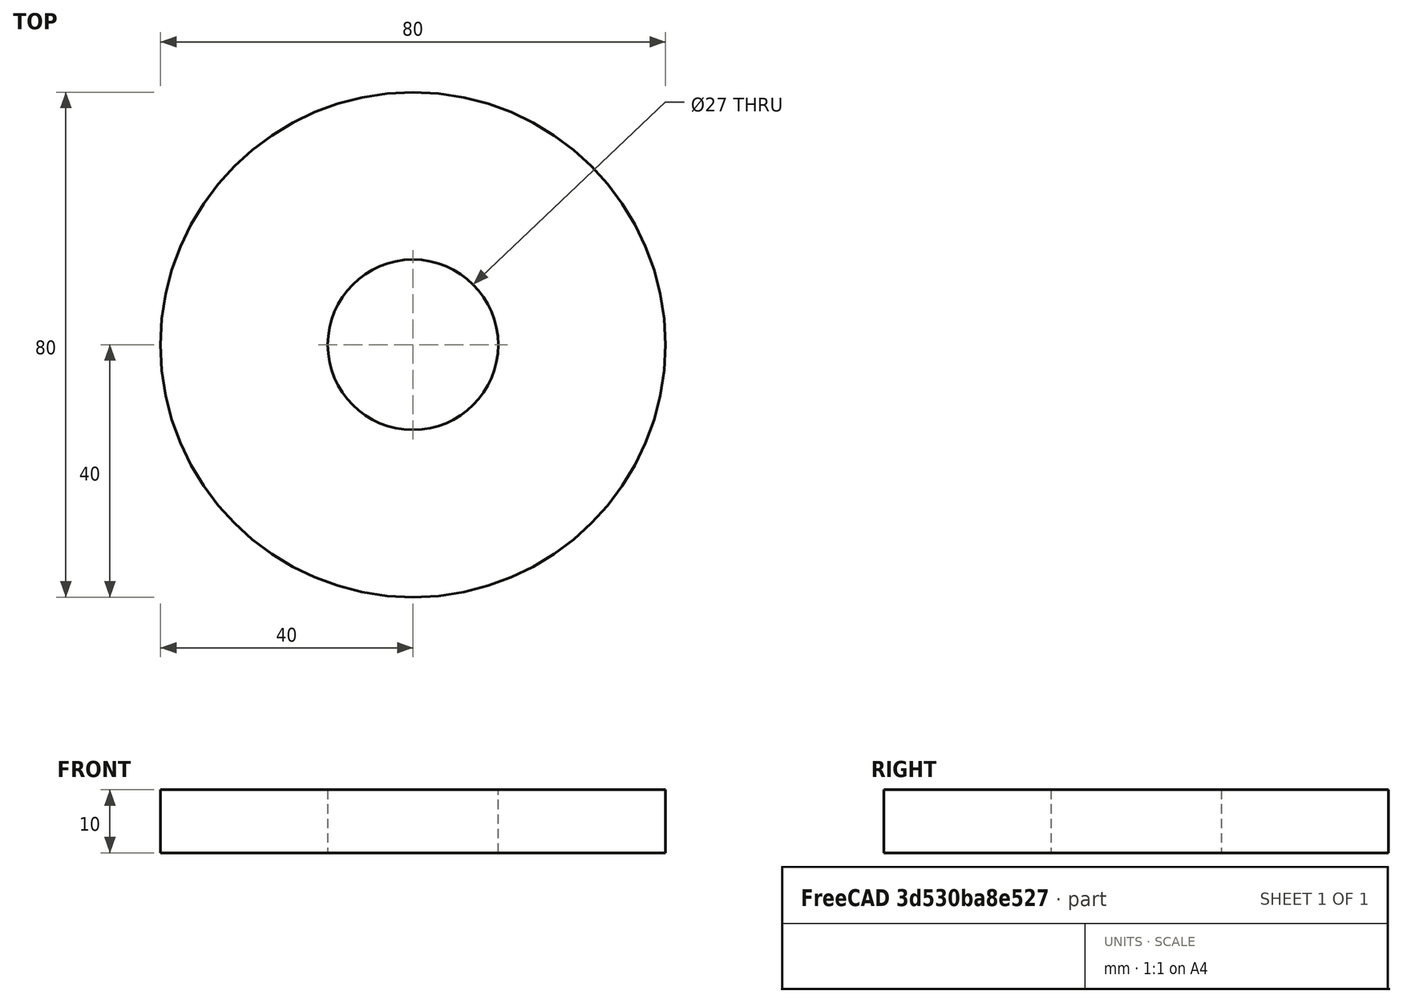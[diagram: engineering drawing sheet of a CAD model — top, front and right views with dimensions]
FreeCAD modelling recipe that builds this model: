
FCSTD DOCUMENT  (FreeCAD 0.19R24276 (Git))
Label: Ring_under_katushka_1
License: All rights reserved
LicenseURL: http://en.wikipedia.org/wiki/All_rights_reserved
objects: Sketcher::SketchObject×1, PartDesign::Pad×1, PartDesign::Body×1
note: 4 computed .brp shape members not serialized (recipe doc carries the construction recipe); baked Part::Feature solids carry a one-line shape summary decoded from their .brp

FEATURE [Sketcher::SketchObject] Sketch
  FullyConstrained = true
  MapMode = 5
  Support = -> [XY_Plane]
  sketch-geometry (2):
    g0: Circle CenterX=0 CenterY=0 CenterZ=0 NormalX=0 NormalY=0 NormalZ=1 AngleXU=0 Radius=13.5
    g1: Circle CenterX=0 CenterY=0 CenterZ=0 NormalX=0 NormalY=0 NormalZ=1 AngleXU=0 Radius=40
  constraints (4):
    c: Coincident(g0,g-1)
    c: Coincident(g1,g0)
    c: Diameter(g0) = 27
    c: Diameter(g1) = 80
FEATURE [PartDesign::Pad] Pad
  Direction = (1,1,1)
  Length = 10
  Length2 = 100
  Profile = -> Sketch
  Type = 0
FEATURE [PartDesign::Body] Body
  Group = -> [Sketch,Pad]
  Origin = -> Origin
  Tip = -> Pad
